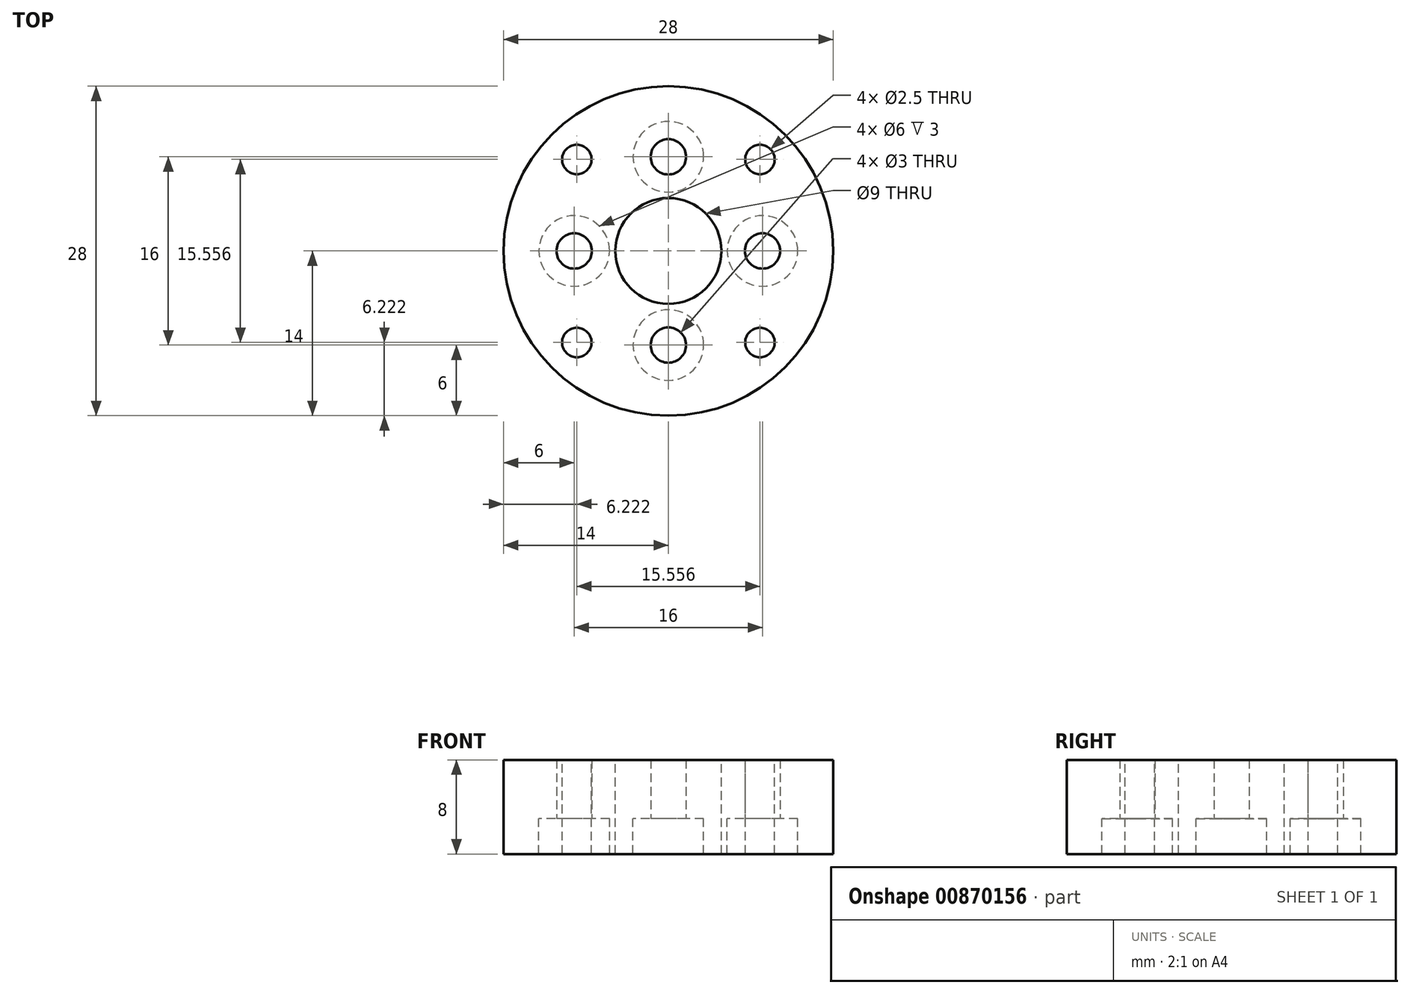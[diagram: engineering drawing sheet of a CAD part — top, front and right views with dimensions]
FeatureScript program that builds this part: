
annotation { "Feature Type Name" : "Feature", "Feature Type Description" : "" }
export const myFeature = defineFeature(function(context is Context, id is Id, definition is map)
    precondition{}
    {
        {
            var Q0;
            Q0=qCreatedBy(makeId("Top.planeOp"),FACE);
            var sketch = newSketch(context, id + "F0", { "sketchPlane" : qUnion([Q0])});
            skCircle(sketch, "E0", {"center": v(0, 0) * mm, "radius": 4.5 * mm});
            skCircle(sketch, "E1", {"center": v(8, 0) * mm, "radius": 1.5 * mm});
            skCircle(sketch, "E2", {"center": v(0, 8) * mm, "radius": 1.5 * mm});
            skCircle(sketch, "E3", {"center": v(-8, 0) * mm, "radius": 1.5 * mm});
            skCircle(sketch, "E4", {"center": v(0, -8) * mm, "radius": 1.5 * mm});
            skLineSegment(sketch, "E5", {"start": v(8, 0) * mm, "end": v(0, 0) * mm, "construction": true});
            skLineSegment(sketch, "E6", {"start": v(0, 0) * mm, "end": v(0, 8) * mm, "construction": true});
            skLineSegment(sketch, "E7", {"start": v(0, 0) * mm, "end": v(-8, 0) * mm, "construction": true});
            skLineSegment(sketch, "E8", {"start": v(0, 0) * mm, "end": v(0, -8) * mm, "construction": true});
            skCircle(sketch, "E9", {"center": v(0, 0) * mm, "radius": 14 * mm});
            skLineSegment(sketch, "E10", {"start": v(0, 0) * mm, "end": v(-7.78, 7.78) * mm, "construction": true});
            skCircle(sketch, "E11", {"center": v(-7.78, 7.78) * mm, "radius": 1.25 * mm});
            skCircle(sketch, "E12", {"center": v(0, 8) * mm, "radius": 3 * mm});
            skCircle(sketch, "E13.1.0", {"center": v(-7.78, -7.78) * mm, "radius": 1.25 * mm});
            skLineSegment(sketch, "E13.1.1", {"start": v(0, 0) * mm, "end": v(-7.78, -7.78) * mm, "construction": true});
            skCircle(sketch, "E13.2.0", {"center": v(7.78, -7.78) * mm, "radius": 1.25 * mm});
            skLineSegment(sketch, "E13.2.1", {"start": v(0, 0) * mm, "end": v(7.78, -7.78) * mm, "construction": true});
            skCircle(sketch, "E13.3.0", {"center": v(7.78, 7.78) * mm, "radius": 1.25 * mm});
            skLineSegment(sketch, "E13.3.1", {"start": v(0, 0) * mm, "end": v(7.78, 7.78) * mm, "construction": true});
            skCircle(sketch, "E14.1.0", {"center": v(-8, 0) * mm, "radius": 3 * mm});
            skCircle(sketch, "E14.2.0", {"center": v(0, -8) * mm, "radius": 3 * mm});
            skCircle(sketch, "E14.3.0", {"center": v(8, 0) * mm, "radius": 3 * mm});
            skSolve(sketch);
        }
        {
            var Q0;
            Q0=makeQuery(id+"F0.imprint","IMPRINT",FACE,{"disambiguationData":[TD([[makeQuery(id+"F0.imprint","IMPRINT",EDGE,{"derivedFrom":sQuery(id+"F0.wireOp",EDGE,"E0")}),-1.0]])]});
            extrude(context, id + "F1", {"entities" : qUnion([Q0]), "oppositeDirection" : true, "depth" : 3 * mm, "offsetDistance" : 25 * mm});
        }
        {
            var Q0;
            Q0=makeQuery(id+"F0.imprint","IMPRINT",FACE,{"disambiguationData":[TD([[makeQuery(id+"F0.imprint","IMPRINT",EDGE,{"derivedFrom":sQuery(id+"F0.wireOp",EDGE,"E3")}),-1.0]])]});
            var Q1;
            Q1=makeQuery(id+"F0.imprint","IMPRINT",FACE,{"disambiguationData":[TD([[makeQuery(id+"F0.imprint","IMPRINT",EDGE,{"derivedFrom":sQuery(id+"F0.wireOp",EDGE,"E2")}),-1.0]])]});
            var Q2;
            Q2=makeQuery(id+"F0.imprint","IMPRINT",FACE,{"disambiguationData":[TD([[makeQuery(id+"F0.imprint","IMPRINT",EDGE,{"derivedFrom":sQuery(id+"F0.wireOp",EDGE,"E1")}),-1.0]])]});
            var Q3;
            Q3=makeQuery(id+"F0.imprint","IMPRINT",FACE,{"disambiguationData":[TD([[makeQuery(id+"F0.imprint","IMPRINT",EDGE,{"derivedFrom":sQuery(id+"F0.wireOp",EDGE,"E4")}),-1.0]])]});
            var Q4;
            Q4=makeQuery(id+"F0.imprint","IMPRINT",FACE,{"disambiguationData":[TD([[makeQuery(id+"F0.imprint","IMPRINT",EDGE,{"derivedFrom":sQuery(id+"F0.wireOp",EDGE,"E0")}),-1.0]])]});
            extrude(context, id + "F2", {"entities" : qUnion([Q0, Q1, Q2, Q3, Q4]), "operationType" : NewBodyOperationType.ADD, "depth" : 5 * mm, "offsetDistance" : 25 * mm});
        }
    });
